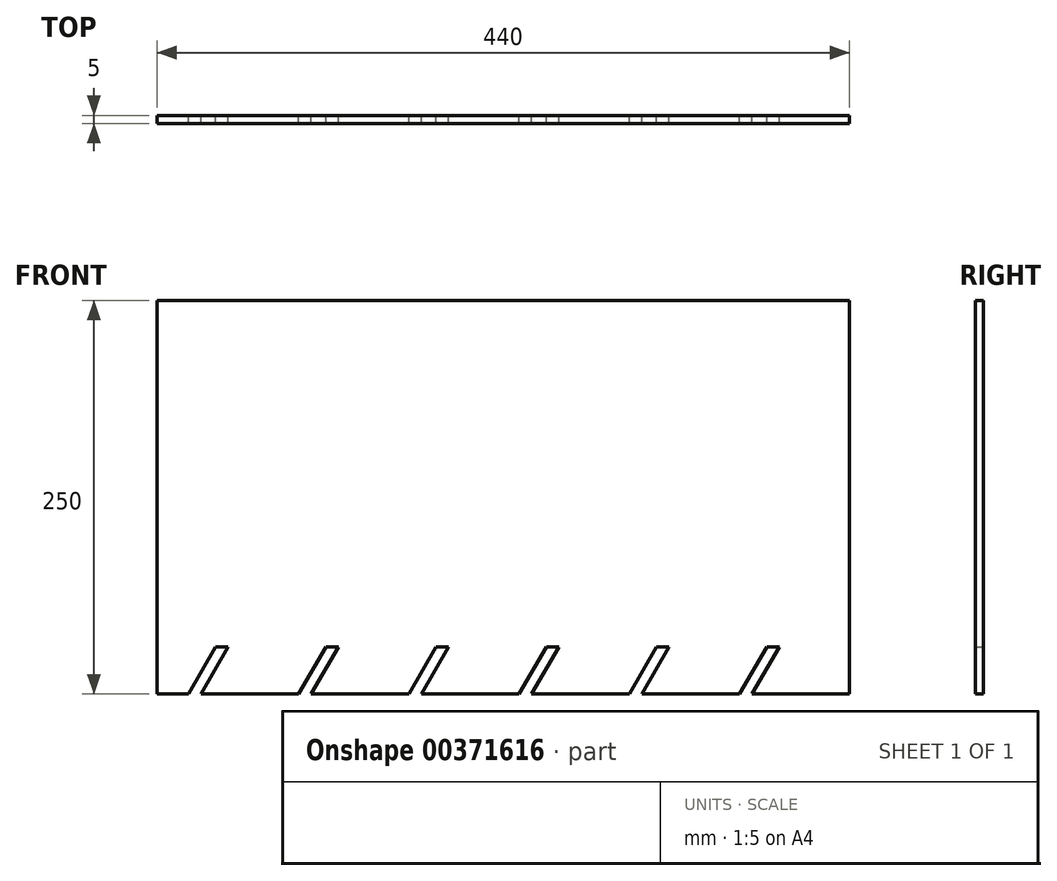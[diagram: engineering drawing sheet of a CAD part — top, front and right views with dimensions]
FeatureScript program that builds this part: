
annotation { "Feature Type Name" : "Feature", "Feature Type Description" : "" }
export const myFeature = defineFeature(function(context is Context, id is Id, definition is map)
    precondition{}
    {
        {
            var Q0;
            Q0=qCreatedBy(makeId("Front.planeOp"),FACE);
            var sketch = newSketch(context, id + "F0", { "sketchPlane" : qUnion([Q0])});
            skLineSegment(sketch, "E0", {"start": v(0, 0) * mm, "end": v(20, 0) * mm});
            skLineSegment(sketch, "E1", {"start": v(20, 0) * mm, "end": v(37.33, 30) * mm});
            skLineSegment(sketch, "E2", {"start": v(37.33, 30) * mm, "end": v(45.33, 30) * mm});
            skLineSegment(sketch, "E3", {"start": v(45.33, 30) * mm, "end": v(28, 0) * mm});
            skLineSegment(sketch, "E4", {"start": v(28, 0) * mm, "end": v(90, 0) * mm});
            skLineSegment(sketch, "E5.1.0.0", {"start": v(90, 0) * mm, "end": v(107.33, 30) * mm});
            skLineSegment(sketch, "E5.1.0.1", {"start": v(115.33, 30) * mm, "end": v(98, 0) * mm});
            skLineSegment(sketch, "E5.1.0.2", {"start": v(98, 0) * mm, "end": v(160, 0) * mm});
            skLineSegment(sketch, "E5.1.0.3", {"start": v(107.33, 30) * mm, "end": v(115.33, 30) * mm});
            skLineSegment(sketch, "E5.2.0.0", {"start": v(160, 0) * mm, "end": v(177.33, 30) * mm});
            skLineSegment(sketch, "E5.2.0.1", {"start": v(185.33, 30) * mm, "end": v(168, 0) * mm});
            skLineSegment(sketch, "E5.2.0.2", {"start": v(168, 0) * mm, "end": v(230, 0) * mm});
            skLineSegment(sketch, "E5.2.0.3", {"start": v(177.33, 30) * mm, "end": v(185.33, 30) * mm});
            skLineSegment(sketch, "E5.3.0.0", {"start": v(230, 0) * mm, "end": v(247.33, 30) * mm});
            skLineSegment(sketch, "E5.3.0.1", {"start": v(255.33, 30) * mm, "end": v(238, 0) * mm});
            skLineSegment(sketch, "E5.3.0.2", {"start": v(238, 0) * mm, "end": v(300, 0) * mm});
            skLineSegment(sketch, "E5.3.0.3", {"start": v(247.33, 30) * mm, "end": v(255.33, 30) * mm});
            skLineSegment(sketch, "E5.4.0.0", {"start": v(300, 0) * mm, "end": v(317.33, 30) * mm});
            skLineSegment(sketch, "E5.4.0.1", {"start": v(325.33, 30) * mm, "end": v(308, 0) * mm});
            skLineSegment(sketch, "E5.4.0.2", {"start": v(308, 0) * mm, "end": v(370, 0) * mm});
            skLineSegment(sketch, "E5.4.0.3", {"start": v(317.33, 30) * mm, "end": v(325.33, 30) * mm});
            skLineSegment(sketch, "E5.5.0.0", {"start": v(370, 0) * mm, "end": v(387.33, 30) * mm});
            skLineSegment(sketch, "E5.5.0.1", {"start": v(395.33, 30) * mm, "end": v(378, 0) * mm});
            skLineSegment(sketch, "E5.5.0.2", {"start": v(378, 0) * mm, "end": v(440, 0) * mm});
            skLineSegment(sketch, "E5.5.0.3", {"start": v(387.33, 30) * mm, "end": v(395.33, 30) * mm});
            skLineSegment(sketch, "E5.direction1", {"start": v(20, 0) * mm, "end": v(90, 0) * mm, "construction": true});
            skLineSegment(sketch, "E6", {"start": v(0, 0) * mm, "end": v(0, 250) * mm});
            skLineSegment(sketch, "E7", {"start": v(0, 250) * mm, "end": v(440, 250) * mm});
            skLineSegment(sketch, "E8", {"start": v(440, 250) * mm, "end": v(440, 0) * mm});
            skSolve(sketch);
        }
        {
            var Q0;
            Q0=makeQuery(id+"F0.imprint","IMPRINT",FACE,{"disambiguationData":[TD([[makeQuery(id+"F0.imprint","IMPRINT",EDGE,{"derivedFrom":sQuery(id+"F0.wireOp",EDGE,"E0")}),1.0]])]});
            extrude(context, id + "F1", {"entities" : qUnion([Q0]), "depth" : 5 * mm});
        }
    });
